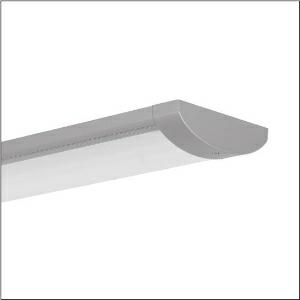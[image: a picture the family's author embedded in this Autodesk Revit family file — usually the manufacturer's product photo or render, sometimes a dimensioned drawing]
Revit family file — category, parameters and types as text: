
# Revit family: tv_20_5xa861d4n0j
name_source: partatom
category: Lighting Fixtures
units: mm (PartAtom-declared; Revit-internal decimal feet)

## family parameters
Cut with Voids When Loaded = No
Host = Face
Light Source = No
Part Type = Normal
Room Calculation Point = No
Round Connector Dimension = Use Diameter
Shared = No

## types (1)
- TV 20 (1 x LED 4000K / CRI = 80 (unbekannt), 3960 lm, 4000K)
    Apparent Load = 37 VA
    CIE Flux Codes = 48 78 95 99 100
    Color Rendering = 80
    Color Temperature = 4000K
    Default Elevation = 1800 mm
    Description = TV 20, vandal-proof luminaire, primary light control with specular reflector, of aluminium, matt, primary optical cover: enclosure, of PC, frosted, light emission: direct distribution, primary light characteristic: symmetric, installation type: surface-mounted, LED, rated luminous flux: 3.960lm, luminous efficacy: 107lm/W, light colour: 840, colour temperature: 4000K, control gear: DALI, mains connection: 230V, AC, 50Hz, rated input power: 37W, luminaire housing, of aluminium, coated, Siteco® metallic grey (DB 702S), with wall and ceiling fixing element, length: 1.261mm, width: 260mm, height: 70mm, mounting height: 2.5..4.0m, protection rating (complete): IP65, insulation class (complete): insulation class I (protective earthing), certification: CE, protection symbol: F, impact resistance: 2x IK10, standard: EN 60598, packaging unit: 1 piece
    Height = 70 mm
    Lamp = 1 x LED 4000K / CRI >= 80 (unbekannt)
    Lamp Light Flux = 3960 lm
    Lamp count = 1
    Length = 1261 mm
    Luminous efficacy = 107 lm/W
    Manufacturer = Siteco
    ModVariant = No
    Model = 5XA861D4N0J
    Mounting Place = Ceiling
    Mounting Type = Surface mounted
    Number of Poles = 1
    OnlyDefault = Yes
    Power Factor = 1
    Product Name = TV 20
    Product group = vandal-proof luminaire
    ProductGroupID = 309
    Protection Class = Protection class I
    Protection Degree = IP 65
    RLX_Detail_Level = 1
    RLX_Emergency_Light_Flux = 0 lm
    RLX_Emergency_Type = 0
    RLX_Emergency_Type_DB = No
    RlxData = <blob elided: 25609 chars, md5=5e85aef8>
    Socket = socket
    Standby Power = 0 W
    System Light Flux = 3960 lm
    System Power = 37 W
    Type Comments = Product without accessories
    Type Image = l_1004809.jpg
    URL = http://relux.com
    VarID = ---
    Voltage = 0 V
    Weight = 0.00 kg
    Width = 260 mm

## geometry (parser evidence)
native form markers: Blend x4, Sweep x9
no freeform markers — native parametric forms only
